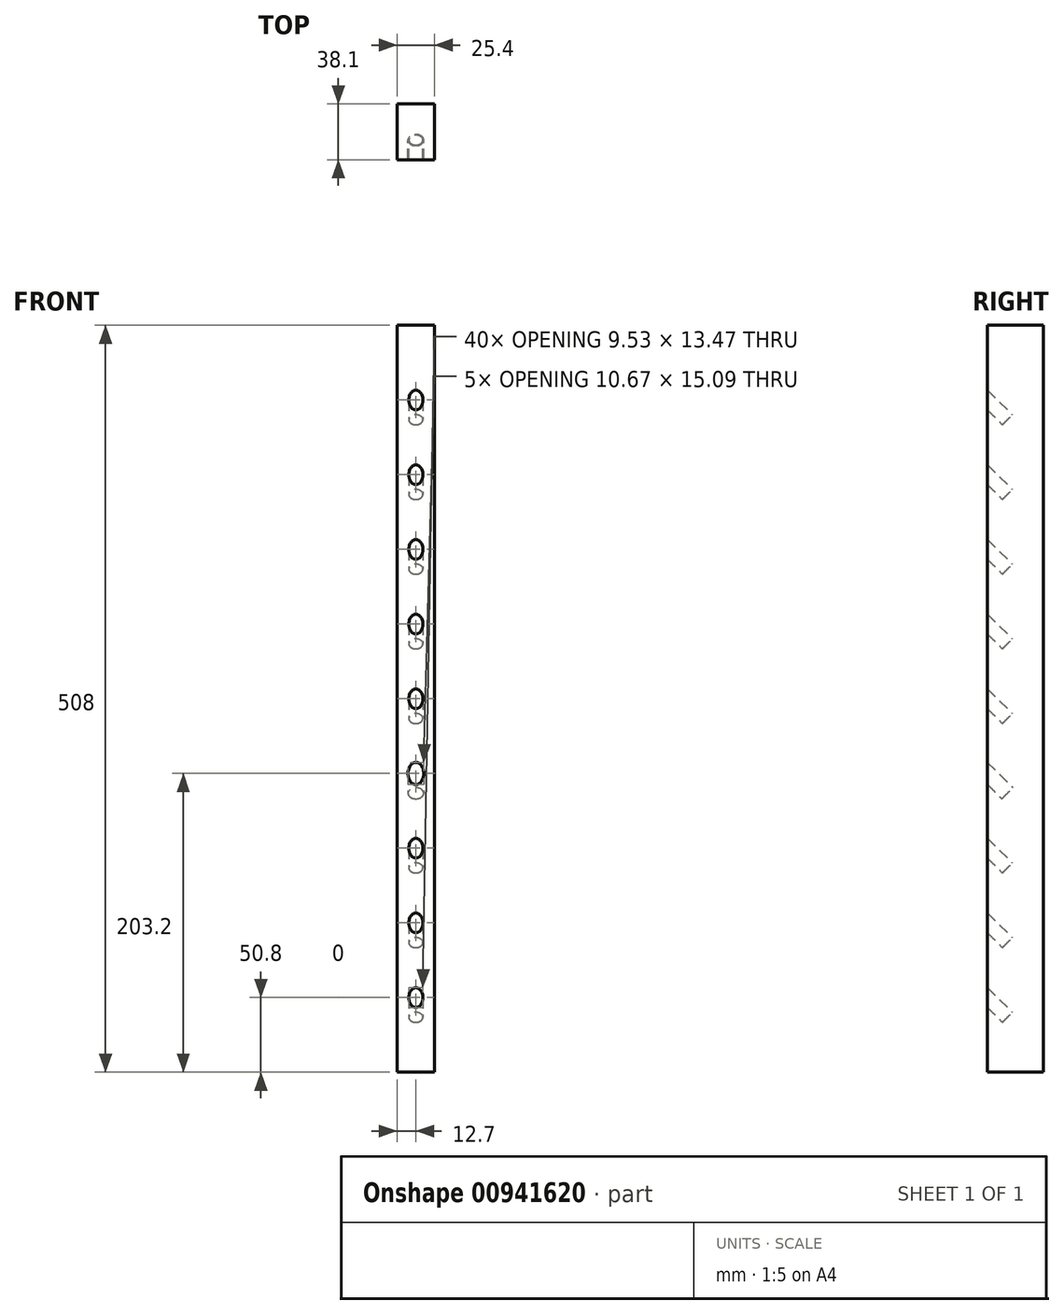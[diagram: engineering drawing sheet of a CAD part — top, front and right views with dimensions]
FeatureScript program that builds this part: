
annotation { "Feature Type Name" : "Feature", "Feature Type Description" : "" }
export const myFeature = defineFeature(function(context is Context, id is Id, definition is map)
    precondition{}
    {
        {
            var Q0;
            Q0=qCreatedBy(makeId("Front.planeOp"),FACE);
            var sketch = newSketch(context, id + "F0", { "sketchPlane" : qUnion([Q0])});
            skLineSegment(sketch, "E0.bottom", {"start": v(12.7, -254) * mm, "end": v(-12.7, -254) * mm});
            skLineSegment(sketch, "E0.top", {"start": v(12.7, 254) * mm, "end": v(-12.7, 254) * mm});
            skLineSegment(sketch, "E0.left", {"start": v(12.7, -254) * mm, "end": v(12.7, 254) * mm});
            skLineSegment(sketch, "E0.right", {"start": v(-12.7, -254) * mm, "end": v(-12.7, 254) * mm});
            skPoint(sketch, "E0.middle", {"position": v(0, 0) * mm});
            skSolve(sketch);
        }
        {
            var Q0;
            Q0=makeQuery(id+"F0.imprint","IMPRINT",FACE,{"disambiguationData":[TD([[makeQuery(id+"F0.imprint","IMPRINT",EDGE,{"derivedFrom":sQuery(id+"F0.wireOp",EDGE,"E0.bottom")}),-1.0]])]});
            extrude(context, id + "F1", {"entities" : qUnion([Q0]), "depth" : 38.1 * mm, "offsetDistance" : 25.4 * mm});
        }
        {
            var Q0;
            Q0=makeQuery(id+"F1.opExtrude","CAP_FACE",FACE,{"disambiguationData":[OSD([sQuery(id+"F0.wireOp",EDGE,"E0.bottom"),sQuery(id+"F0.wireOp",EDGE,"E0.top"),sQuery(id+"F0.wireOp",EDGE,"E0.left"),sQuery(id+"F0.wireOp",EDGE,"E0.right")])],"isStart":false});
            var sketch = newSketch(context, id + "F2", { "sketchPlane" : qUnion([Q0])});
            skPoint(sketch, "E1", {"position": v(0, 203.2) * mm});
            skPoint(sketch, "E1.positionSnap0", {"position": v(0, 254) * mm});
            skPoint(sketch, "E2", {"position": v(0, 152.4) * mm});
            skPoint(sketch, "E3", {"position": v(0, 101.6) * mm});
            skPoint(sketch, "E4", {"position": v(0, 50.8) * mm});
            skPoint(sketch, "E5", {"position": v(0, 0) * mm});
            skPoint(sketch, "E6", {"position": v(0, -50.8) * mm});
            skPoint(sketch, "E7", {"position": v(0, -101.6) * mm});
            skPoint(sketch, "E8", {"position": v(0, -152.4) * mm});
            skPoint(sketch, "E9", {"position": v(0, -203.2) * mm});
            skLineSegment(sketch, "E10", {"start": v(-12.7, 203.2) * mm, "end": v(12.7, 203.2) * mm});
            skLineSegment(sketch, "E11", {"start": v(-12.7, 152.4) * mm, "end": v(12.7, 152.4) * mm});
            skLineSegment(sketch, "E12", {"start": v(-12.7, 101.6) * mm, "end": v(12.7, 101.6) * mm});
            skLineSegment(sketch, "E13", {"start": v(-12.7, 50.8) * mm, "end": v(12.7, 50.8) * mm});
            skLineSegment(sketch, "E14", {"start": v(-12.7, 0) * mm, "end": v(12.7, 0) * mm});
            skLineSegment(sketch, "E15", {"start": v(-12.7, -50.8) * mm, "end": v(12.7, -50.8) * mm});
            skLineSegment(sketch, "E16", {"start": v(-12.7, -101.6) * mm, "end": v(12.7, -101.6) * mm});
            skLineSegment(sketch, "E17", {"start": v(-12.7, -152.4) * mm, "end": v(12.7, -152.4) * mm});
            skLineSegment(sketch, "E18", {"start": v(-12.7, -203.2) * mm, "end": v(12.7, -203.2) * mm});
            skSolve(sketch);
        }
        {
            var Q0;
            Q0=sQuery(id+"F2.wireOp",EDGE,"E10");
            cPlane(context, id + "F3", {"entities" : qUnion([Q0]), "cplaneType" : CPlaneType.LINE_ANGLE, "offset" : 25.4 * mm, "angle" : 135 * degree, "width" : 152.4 * mm, "height" : 152.4 * mm});
        }
        {
            var Q0;
            Q0=qCreatedBy(id+"F3.planeOp",FACE);
            var sketch = newSketch(context, id + "F4", { "sketchPlane" : qUnion([Q0])});
            skCircle(sketch, "E19", {"center": v(0, 116.74) * mm, "radius": 4.76 * mm});
            skSolve(sketch);
        }
        {
            var Q0;
            Q0=sQuery(id+"F2.wireOp",EDGE,"E11");
            cPlane(context, id + "F5", {"entities" : qUnion([Q0]), "cplaneType" : CPlaneType.LINE_ANGLE, "offset" : 25.4 * mm, "angle" : 135 * degree, "width" : 152.4 * mm, "height" : 152.4 * mm});
        }
        {
            var Q0;
            Q0=qCreatedBy(id+"F5.planeOp",FACE);
            var sketch = newSketch(context, id + "F6", { "sketchPlane" : qUnion([Q0])});
            skCircle(sketch, "E20", {"center": v(0, 80.82) * mm, "radius": 4.76 * mm});
            skSolve(sketch);
        }
        {
            var Q0;
            Q0=sQuery(id+"F2.wireOp",EDGE,"E12");
            cPlane(context, id + "F7", {"entities" : qUnion([Q0]), "cplaneType" : CPlaneType.LINE_ANGLE, "offset" : 25.4 * mm, "angle" : 135 * degree, "width" : 152.4 * mm, "height" : 152.4 * mm});
        }
        {
            var Q0;
            Q0=qCreatedBy(id+"F7.planeOp",FACE);
            var sketch = newSketch(context, id + "F8", { "sketchPlane" : qUnion([Q0])});
            skCircle(sketch, "E21", {"center": v(0, 44.9) * mm, "radius": 4.76 * mm});
            skSolve(sketch);
        }
        {
            var Q0;
            Q0=sQuery(id+"F2.wireOp",EDGE,"E13");
            cPlane(context, id + "F9", {"entities" : qUnion([Q0]), "cplaneType" : CPlaneType.LINE_ANGLE, "offset" : 25.4 * mm, "angle" : 135 * degree, "width" : 152.4 * mm, "height" : 152.4 * mm});
        }
        {
            var Q0;
            Q0=qCreatedBy(id+"F9.planeOp",FACE);
            var sketch = newSketch(context, id + "F10", { "sketchPlane" : qUnion([Q0])});
            skCircle(sketch, "E22", {"center": v(0, 8.98) * mm, "radius": 4.76 * mm});
            skSolve(sketch);
        }
        {
            var Q0;
            Q0=sQuery(id+"F2.wireOp",EDGE,"E14");
            cPlane(context, id + "F11", {"entities" : qUnion([Q0]), "cplaneType" : CPlaneType.LINE_ANGLE, "offset" : 25.4 * mm, "angle" : 135 * degree, "width" : 152.4 * mm, "height" : 152.4 * mm});
        }
        {
            var Q0;
            Q0=qCreatedBy(id+"F11.planeOp",FACE);
            var sketch = newSketch(context, id + "F12", { "sketchPlane" : qUnion([Q0])});
            skCircle(sketch, "E23", {"center": v(0, -26.94) * mm, "radius": 4.76 * mm});
            skSolve(sketch);
        }
        {
            var Q0;
            Q0=sQuery(id+"F2.wireOp",EDGE,"E15");
            cPlane(context, id + "F13", {"entities" : qUnion([Q0]), "cplaneType" : CPlaneType.LINE_ANGLE, "offset" : 25.4 * mm, "angle" : 135 * degree, "width" : 152.4 * mm, "height" : 152.4 * mm});
        }
        {
            var Q0;
            Q0=qCreatedBy(id+"F13.planeOp",FACE);
            var sketch = newSketch(context, id + "F14", { "sketchPlane" : qUnion([Q0])});
            skCircle(sketch, "E24", {"center": v(0, -62.86) * mm, "radius": 5.34 * mm});
            skSolve(sketch);
        }
        {
            var Q0;
            Q0=sQuery(id+"F2.wireOp",EDGE,"E16");
            cPlane(context, id + "F15", {"entities" : qUnion([Q0]), "cplaneType" : CPlaneType.LINE_ANGLE, "offset" : 25.4 * mm, "angle" : 135 * degree, "width" : 152.4 * mm, "height" : 152.4 * mm});
        }
        {
            var Q0;
            Q0=qCreatedBy(id+"F15.planeOp",FACE);
            var sketch = newSketch(context, id + "F16", { "sketchPlane" : qUnion([Q0])});
            skCircle(sketch, "E25", {"center": v(0, -98.78) * mm, "radius": 4.76 * mm});
            skSolve(sketch);
        }
        {
            var Q0;
            Q0=sQuery(id+"F2.wireOp",EDGE,"E17");
            cPlane(context, id + "F17", {"entities" : qUnion([Q0]), "cplaneType" : CPlaneType.LINE_ANGLE, "offset" : 25.4 * mm, "angle" : 135 * degree, "width" : 152.4 * mm, "height" : 152.4 * mm});
        }
        {
            var Q0;
            Q0=qCreatedBy(id+"F17.planeOp",FACE);
            var sketch = newSketch(context, id + "F18", { "sketchPlane" : qUnion([Q0])});
            skCircle(sketch, "E26", {"center": v(0, -134.7) * mm, "radius": 4.76 * mm});
            skSolve(sketch);
        }
        {
            var Q0;
            Q0=sQuery(id+"F2.wireOp",EDGE,"E18");
            cPlane(context, id + "F19", {"entities" : qUnion([Q0]), "cplaneType" : CPlaneType.LINE_ANGLE, "offset" : 25.4 * mm, "angle" : 135 * degree, "width" : 152.4 * mm, "height" : 152.4 * mm});
        }
        {
            var Q0;
            Q0=qCreatedBy(id+"F19.planeOp",FACE);
            var sketch = newSketch(context, id + "F20", { "sketchPlane" : qUnion([Q0])});
            skCircle(sketch, "E27", {"center": v(0, -170.62) * mm, "radius": 4.76 * mm});
            skSolve(sketch);
        }
        {
            var Q0;
            Q0=makeQuery(id+"F4.imprint","IMPRINT",FACE,{"disambiguationData":[TD([[makeQuery(id+"F4.imprint","IMPRINT",EDGE,{"derivedFrom":sQuery(id+"F4.wireOp",EDGE,"E19")}),1.0]])]});
            var Q1;
            Q1=makeQuery(id+"F6.imprint","IMPRINT",FACE,{"disambiguationData":[TD([[makeQuery(id+"F6.imprint","IMPRINT",EDGE,{"derivedFrom":sQuery(id+"F6.wireOp",EDGE,"E20")}),1.0]])]});
            var Q2;
            Q2=makeQuery(id+"F8.imprint","IMPRINT",FACE,{"disambiguationData":[TD([[makeQuery(id+"F8.imprint","IMPRINT",EDGE,{"derivedFrom":sQuery(id+"F8.wireOp",EDGE,"E21")}),1.0]])]});
            var Q3;
            Q3=makeQuery(id+"F10.imprint","IMPRINT",FACE,{"disambiguationData":[TD([[makeQuery(id+"F10.imprint","IMPRINT",EDGE,{"derivedFrom":sQuery(id+"F10.wireOp",EDGE,"E22")}),1.0]])]});
            var Q4;
            Q4=makeQuery(id+"F12.imprint","IMPRINT",FACE,{"disambiguationData":[TD([[makeQuery(id+"F12.imprint","IMPRINT",EDGE,{"derivedFrom":sQuery(id+"F12.wireOp",EDGE,"E23")}),1.0]])]});
            var Q5;
            Q5=makeQuery(id+"F14.imprint","IMPRINT",FACE,{"disambiguationData":[TD([[makeQuery(id+"F14.imprint","IMPRINT",EDGE,{"derivedFrom":sQuery(id+"F14.wireOp",EDGE,"E24")}),1.0]])]});
            var Q6;
            Q6=makeQuery(id+"F16.imprint","IMPRINT",FACE,{"disambiguationData":[TD([[makeQuery(id+"F16.imprint","IMPRINT",EDGE,{"derivedFrom":sQuery(id+"F16.wireOp",EDGE,"E25")}),1.0]])]});
            var Q7;
            Q7=makeQuery(id+"F18.imprint","IMPRINT",FACE,{"disambiguationData":[TD([[makeQuery(id+"F18.imprint","IMPRINT",EDGE,{"derivedFrom":sQuery(id+"F18.wireOp",EDGE,"E26")}),1.0]])]});
            var Q8;
            Q8=makeQuery(id+"F20.imprint","IMPRINT",FACE,{"disambiguationData":[TD([[makeQuery(id+"F20.imprint","IMPRINT",EDGE,{"derivedFrom":sQuery(id+"F20.wireOp",EDGE,"E27")}),1.0]])]});
            extrude(context, id + "F21", {"entities" : qUnion([Q0, Q1, Q2, Q3, Q4, Q5, Q6, Q7, Q8]), "operationType" : NewBodyOperationType.REMOVE, "endBound" : BoundingType.SYMMETRIC, "depth" : 38.1 * mm, "offsetDistance" : 25.4 * mm});
        }
    });
